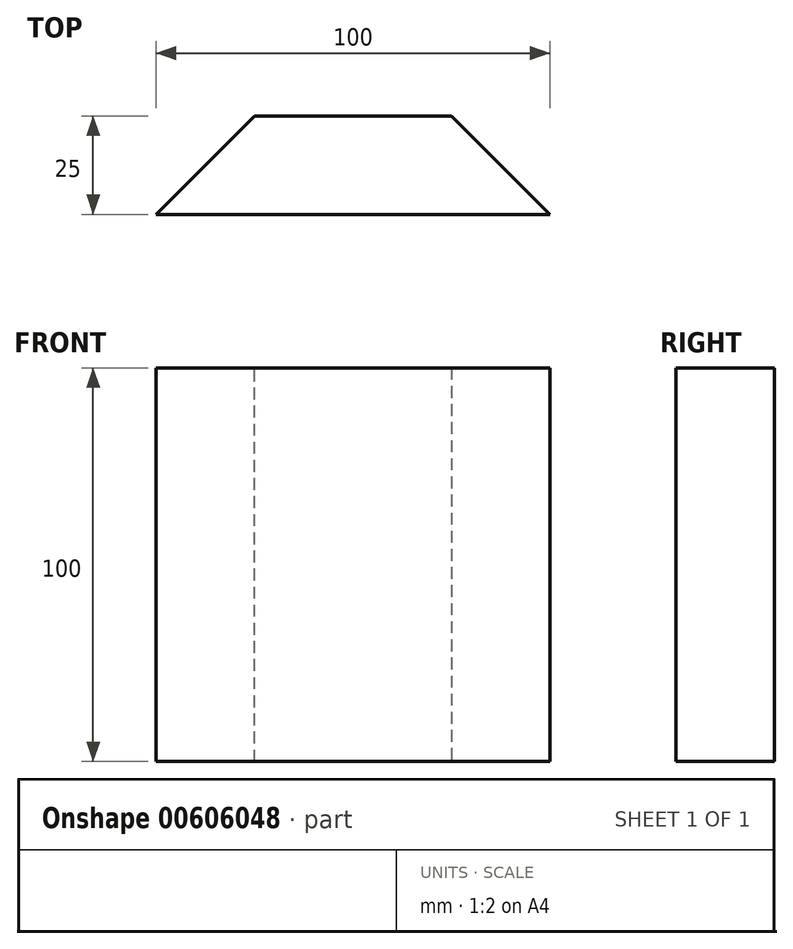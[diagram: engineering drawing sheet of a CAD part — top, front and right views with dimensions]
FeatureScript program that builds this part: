
annotation { "Feature Type Name" : "Feature", "Feature Type Description" : "" }
export const myFeature = defineFeature(function(context is Context, id is Id, definition is map)
    precondition{}
    {
        {
            var Q0;
            Q0=qCreatedBy(makeId("Front.planeOp"),FACE);
            var sketch = newSketch(context, id + "F0", { "sketchPlane" : qUnion([Q0])});
            skLineSegment(sketch, "E0.bottom", {"start": v(50, -50) * mm, "end": v(-50, -50) * mm});
            skLineSegment(sketch, "E0.top", {"start": v(50, 50) * mm, "end": v(-50, 50) * mm});
            skLineSegment(sketch, "E0.left", {"start": v(50, -50) * mm, "end": v(50, 50) * mm});
            skLineSegment(sketch, "E0.right", {"start": v(-50, -50) * mm, "end": v(-50, 50) * mm});
            skPoint(sketch, "E0.middle", {"position": v(0, 0) * mm});
            skSolve(sketch);
        }
        {
            var Q0;
            Q0=makeQuery(id+"F0.imprint","IMPRINT",FACE,{"disambiguationData":[TD([[makeQuery(id+"F0.imprint","IMPRINT",EDGE,{"derivedFrom":sQuery(id+"F0.wireOp",EDGE,"E0.bottom")}),-1.0]])]});
            extrude(context, id + "F1", {"entities" : qUnion([Q0]), "oppositeDirection" : true, "depth" : 25 * mm, "offsetDistance" : 25 * mm});
        }
        {
            var Q0;
            Q0=makeQuery(id+"F1.opExtrude","CAP_EDGE",EDGE,{"disambiguationData":[OSD([sQuery(id+"F0.wireOp",EDGE,"E0.left")])],"isStart":false});
            var Q1;
            Q1=makeQuery(id+"F1.opExtrude","CAP_EDGE",EDGE,{"disambiguationData":[OSD([sQuery(id+"F0.wireOp",EDGE,"E0.right")])],"isStart":false});
            chamfer(context, id + "F2", {"entities" : qUnion([Q0, Q1]), "width" : 25 * mm, "tangentPropagation" : true});
        }
    });
